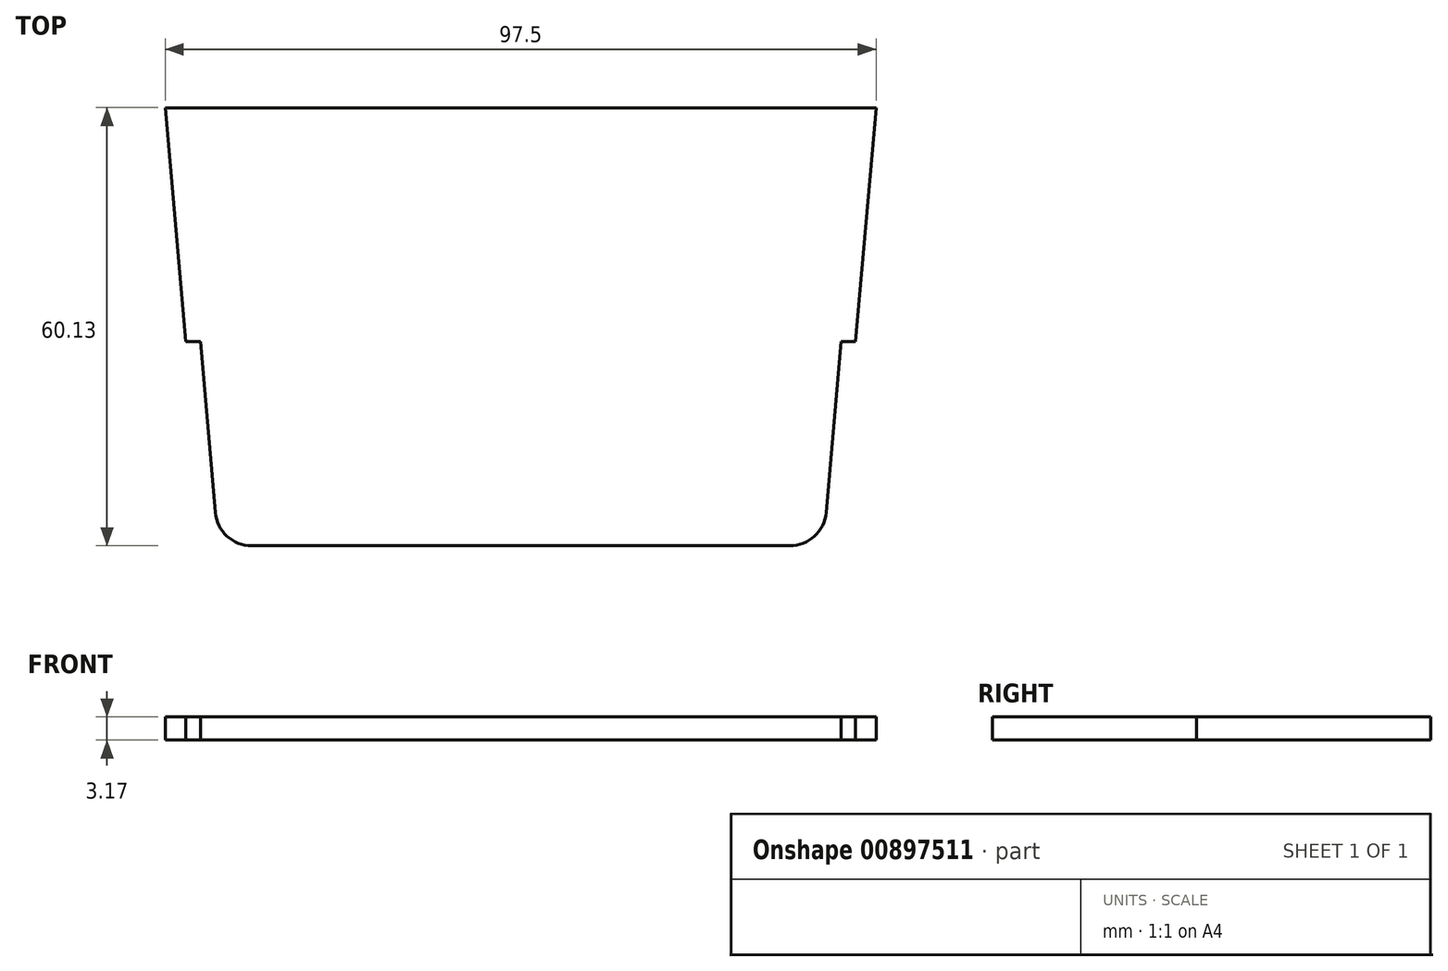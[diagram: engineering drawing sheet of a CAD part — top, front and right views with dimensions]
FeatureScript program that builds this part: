
annotation { "Feature Type Name" : "Feature", "Feature Type Description" : "" }
export const myFeature = defineFeature(function(context is Context, id is Id, definition is map)
    precondition{}
    {
        {
            var Q0;
            Q0=qCreatedBy(makeId("Top.planeOp"),FACE);
            var sketch = newSketch(context, id + "F0", { "sketchPlane" : qUnion([Q0])});
            skLineSegment(sketch, "E0", {"start": v(-48.75, 14.64) * mm, "end": v(48.75, 14.64) * mm});
            skLineSegment(sketch, "E1", {"start": v(45.94, -17.49) * mm, "end": v(43.94, -17.49) * mm});
            skLineSegment(sketch, "E2", {"start": v(43.94, -17.49) * mm, "end": v(41.5, -45.49) * mm});
            skLineSegment(sketch, "E3", {"start": v(41.5, -45.49) * mm, "end": v(0, -45.49) * mm});
            skLineSegment(sketch, "E4", {"start": v(0, -45.49) * mm, "end": v(-41.5, -45.49) * mm});
            skLineSegment(sketch, "E5", {"start": v(-41.5, -45.49) * mm, "end": v(-43.94, -17.49) * mm});
            skLineSegment(sketch, "E6", {"start": v(-43.94, -17.49) * mm, "end": v(-45.94, -17.49) * mm});
            skLineSegment(sketch, "E7", {"start": v(-45.94, -17.49) * mm, "end": v(-48.75, 14.64) * mm});
            skLineSegment(sketch, "E8", {"start": v(45.94, -17.49) * mm, "end": v(48.75, 14.64) * mm});
            skLineSegment(sketch, "E9", {"start": v(0, -45.49) * mm, "end": v(0, 0) * mm, "construction": true});
            skSolve(sketch);
        }
        {
            var Q0;
            Q0=makeQuery(id+"F0.imprint","IMPRINT",FACE,{"disambiguationData":[TD([[makeQuery(id+"F0.imprint","IMPRINT",EDGE,{"derivedFrom":sQuery(id+"F0.wireOp",EDGE,"E0")}),-1.0]])]});
            extrude(context, id + "F1", {"entities" : qUnion([Q0]), "depth" : 3.17 * mm, "offsetDistance" : 25 * mm});
        }
        {
            var Q0;
            Q0=makeQuery(id+"F1.opExtrude","SWEPT_EDGE",EDGE,{"disambiguationData":[OSD([sQuery(id+"F0.wireOp",EDGE,"E4"),sQuery(id+"F0.wireOp",EDGE,"E5")])]});
            var Q1;
            Q1=makeQuery(id+"F1.opExtrude","SWEPT_EDGE",EDGE,{"disambiguationData":[OSD([sQuery(id+"F0.wireOp",EDGE,"E2"),sQuery(id+"F0.wireOp",EDGE,"E3")])]});
            fillet(context, id + "F2", {"entities" : qUnion([Q0, Q1]), "radius" : 5 * mm, "tangentPropagation" : true, "allowEdgeOverflow" : false});
        }
    });
